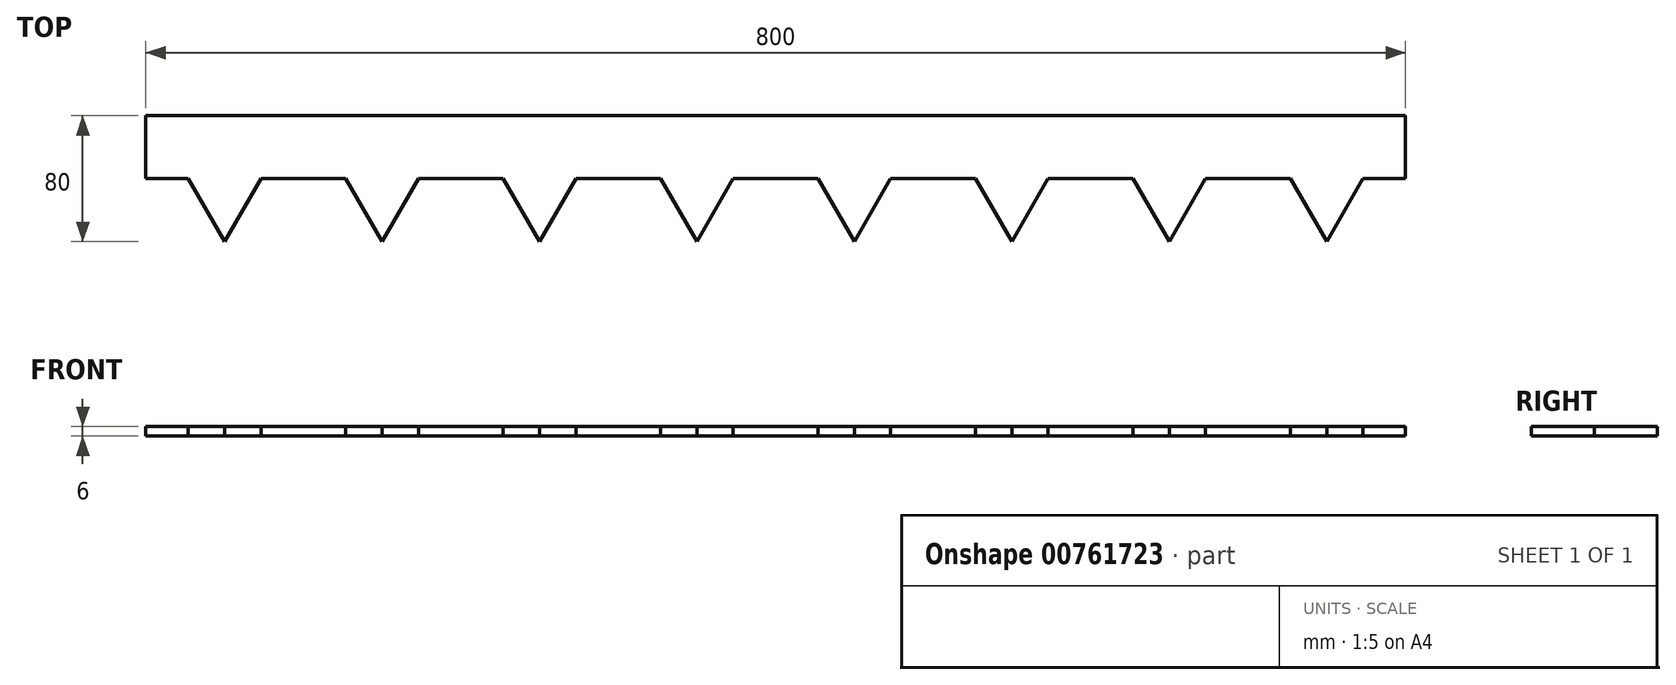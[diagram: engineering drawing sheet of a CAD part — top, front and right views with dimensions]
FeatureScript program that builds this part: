
annotation { "Feature Type Name" : "Feature", "Feature Type Description" : "" }
export const myFeature = defineFeature(function(context is Context, id is Id, definition is map)
    precondition{}
    {
        {
            var Q0;
            Q0=qCreatedBy(makeId("Top.planeOp"),FACE);
            var sketch = newSketch(context, id + "F0", { "sketchPlane" : qUnion([Q0])});
            skLineSegment(sketch, "E0", {"start": v(0, 0) * mm, "end": v(800, 0) * mm});
            skLineSegment(sketch, "E1", {"start": v(800, 0) * mm, "end": v(800, -40) * mm});
            skLineSegment(sketch, "E2", {"start": v(800, -40) * mm, "end": v(0, -40) * mm});
            skLineSegment(sketch, "E3", {"start": v(0, -40) * mm, "end": v(0, 0) * mm});
            skLineSegment(sketch, "E4", {"start": v(50, -21) * mm, "end": v(50, -80) * mm, "construction": true});
            skLineSegment(sketch, "E5", {"start": v(50, -80) * mm, "end": v(80.59, -27.02) * mm});
            skLineSegment(sketch, "E6.MirrorCS", {"start": v(50, -80) * mm, "end": v(19.41, -27.02) * mm});
            skLineSegment(sketch, "E7.1.0.0", {"start": v(150, -80) * mm, "end": v(119.41, -27.02) * mm});
            skLineSegment(sketch, "E7.1.0.1", {"start": v(150, -80) * mm, "end": v(180.59, -27.02) * mm});
            skLineSegment(sketch, "E7.2.0.0", {"start": v(250, -80) * mm, "end": v(219.41, -27.02) * mm});
            skLineSegment(sketch, "E7.2.0.1", {"start": v(250, -80) * mm, "end": v(280.59, -27.02) * mm});
            skLineSegment(sketch, "E7.3.0.0", {"start": v(350, -80) * mm, "end": v(319.41, -27.02) * mm});
            skLineSegment(sketch, "E7.3.0.1", {"start": v(350, -80) * mm, "end": v(380.59, -27.02) * mm});
            skLineSegment(sketch, "E7.4.0.0", {"start": v(450, -80) * mm, "end": v(419.41, -27.02) * mm});
            skLineSegment(sketch, "E7.4.0.1", {"start": v(450, -80) * mm, "end": v(480.59, -27.02) * mm});
            skLineSegment(sketch, "E7.5.0.0", {"start": v(550, -80) * mm, "end": v(519.41, -27.02) * mm});
            skLineSegment(sketch, "E7.5.0.1", {"start": v(550, -80) * mm, "end": v(580.59, -27.02) * mm});
            skLineSegment(sketch, "E7.6.0.0", {"start": v(650, -80) * mm, "end": v(619.41, -27.02) * mm});
            skLineSegment(sketch, "E7.6.0.1", {"start": v(650, -80) * mm, "end": v(680.59, -27.02) * mm});
            skLineSegment(sketch, "E7.7.0.0", {"start": v(750, -80) * mm, "end": v(719.41, -27.02) * mm});
            skLineSegment(sketch, "E7.7.0.1", {"start": v(750, -80) * mm, "end": v(780.59, -27.02) * mm});
            skLineSegment(sketch, "E7.direction1", {"start": v(50, -80) * mm, "end": v(150, -80) * mm, "construction": true});
            skSolve(sketch);
        }
        {
            var Q0;
            Q0 = qSketchRegion(id + "F0", true);
            extrude(context, id + "F1", {"entities" : qUnion([Q0]), "depth" : 6 * mm, "offsetDistance" : 25 * mm});
        }
    });
